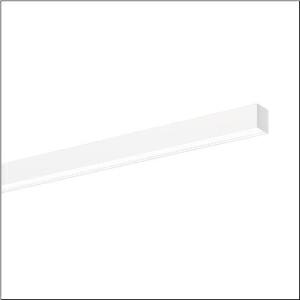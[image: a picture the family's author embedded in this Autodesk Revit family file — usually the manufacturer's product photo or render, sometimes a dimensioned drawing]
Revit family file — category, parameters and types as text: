
# Revit family: silica_r__21_51mx23db35wb_106f
name_source: partatom
category: Lighting Fixtures
units: mm (PartAtom-declared; Revit-internal decimal feet)

## family parameters
Cut with Voids When Loaded = No
Host = Face
Light Source = No
Part Type = Normal
Room Calculation Point = No
Round Connector Dimension = Use Diameter
Shared = No

## types (1)
- --- (1 x LED, 4100 lm, 30.1 W, 3000K)
    Apparent Load = 30 VA
    CIE Flux Codes = 78 96 99 100 100
    Color Rendering = 80
    Color Temperature = 3000K
    Default Elevation = 1800 mm
    Description = Silica® 21, office luminaire, primary optical cover: prismatic diffuser, of PMMA, CAT 2 (L<= 3000cd/m²), light emission: direct distribution, primary light characteristic: symmetric, installation type: surface-mounted, LED, rated luminous flux: 4.100lm, luminous efficacy: 136lm/W, light colour: 830, colour temperature: 3000K, with terminal, 3+2-pole, max. 2.5mm², mains connection: 220..240V, AC, 50/60Hz, rated input power: 30.1W, luminaire housing, of aluminium, traffic white (RAL 9016), length: 1.504mm, width: 53mm, height: 53mm, protection rating (complete): IP20, insulation class (complete): insulation class I (protective earthing), certification: CE, permissible operating ambient temperature: 0..+35°C, standard: EN 50419, packaging unit: 1 piece
    Height = 0 mm  [stored 0 ft]
    Lamp = 1 x LED
    Lamp Light Flux = 4100 lm
    Lamp Power = 30.1 W
    Lamp count = 1
    Length = 1504 mm
    Luminous efficacy = 136 lm/W
    Manufacturer = Siteco
    ModVariant = No
    Model = 51MX23DB35WB
    Mounting Place = Ceiling
    Mounting Type = Recessed
    Number of Poles = 1
    OnlyDefault = Yes
    Power Factor = 1
    Product Name = Silica® 21
    Product group = office luminaire | ceiling recessed
    ProductGroupID = 401
    Protection Class = Protection class I
    Protection Degree = IP 20
    RLX_Detail_Level = 1
    RLX_Emergency_Light_Flux = 0 lm
    RLX_Emergency_Type = 0
    RLX_Emergency_Type_DB = No
    RlxData = <blob elided: 18725 chars, md5=430e95f7>
    Socket = socket
    Standby Power = 0 W
    System Light Flux = 4100 lm
    System Power = 30 W
    Type Comments = factory setting: luminous flux: 100 % | dim-lin: 254 | 345 mA
    Type Image = l_1297777.jpg
    URL = http://relux.com
    VarID = @adj_050159
    Voltage = 0 V
    Weight = 0.00 kg
    Width = 53 mm

note: [stored X ft] marks values corroborated as IEEE doubles in the binary element streams (Revit-internal decimal feet)

## geometry (parser evidence)
native form markers: Blend x4, Sweep x12
no freeform markers — native parametric forms only
